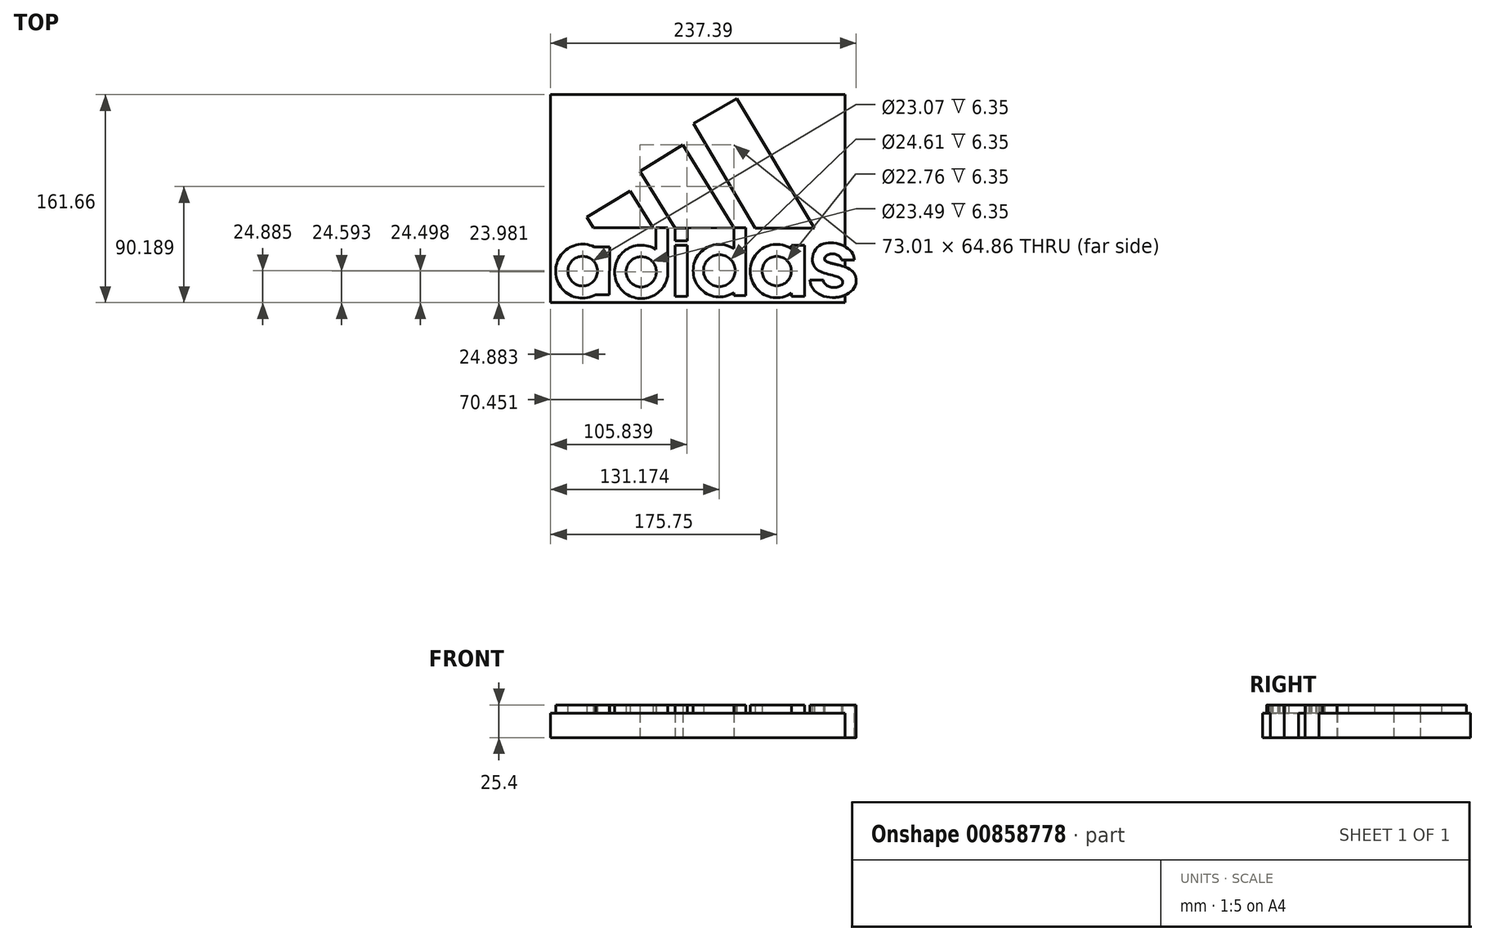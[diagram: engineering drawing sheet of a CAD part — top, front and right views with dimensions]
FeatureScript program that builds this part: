
annotation { "Feature Type Name" : "Feature", "Feature Type Description" : "" }
export const myFeature = defineFeature(function(context is Context, id is Id, definition is map)
    precondition{}
    {
        {
            var Q0;
            Q0=qCreatedBy(makeId("Top.planeOp"),FACE);
            var sketch = newSketch(context, id + "F0", { "sketchPlane" : qUnion([Q0])});
            skLineSegment(sketch, "E0", {"start": v(-125.71, -21.71) * mm, "end": v(-120.74, -29.97) * mm});
            skLineSegment(sketch, "E1", {"start": v(-120.74, -29.97) * mm, "end": v(-74.34, -29.97) * mm});
            skLineSegment(sketch, "E2", {"start": v(-125.71, -21.71) * mm, "end": v(-92.06, -1.43) * mm});
            skLineSegment(sketch, "E3", {"start": v(-92.06, -1.43) * mm, "end": v(-74.34, -30.02) * mm});
            skLineSegment(sketch, "E4", {"start": v(-84.5, 13.67) * mm, "end": v(-57.14, -30.51) * mm});
            skLineSegment(sketch, "E5", {"start": v(-84.5, 13.67) * mm, "end": v(-51.1, 34.35) * mm});
            skLineSegment(sketch, "E6", {"start": v(-51.1, 34.35) * mm, "end": v(-11.49, -30.13) * mm});
            skLineSegment(sketch, "E7", {"start": v(-57.14, -30.51) * mm, "end": v(-11.49, -30.13) * mm});
            skLineSegment(sketch, "E8", {"start": v(-42.92, 50.88) * mm, "end": v(-9.05, 70.16) * mm});
            skCircle(sketch, "E9", {"center": v(-128.95, -63.77) * mm, "radius": 11.53 * mm});
            skCircle(sketch, "E10", {"center": v(-128.95, -63.77) * mm, "radius": 20.97 * mm});
            skLineSegment(sketch, "E11", {"start": v(-107.87, -44.9) * mm, "end": v(-108.07, -82.07) * mm});
            skLineSegment(sketch, "E12", {"start": v(-107.87, -44.9) * mm, "end": v(-119.94, -44.84) * mm});
            skLineSegment(sketch, "E13", {"start": v(-108.07, -82.07) * mm, "end": v(-118.6, -82) * mm});
            skLineSegment(sketch, "E14.bottom", {"start": v(-71.98, -30.02) * mm, "end": v(-62.96, -30.02) * mm});
            skLineSegment(sketch, "E14.top", {"start": v(-71.98, -83.35) * mm, "end": v(-62.96, -83.35) * mm});
            skLineSegment(sketch, "E14.left", {"start": v(-71.98, -30.02) * mm, "end": v(-71.98, -83.35) * mm});
            skLineSegment(sketch, "E14.right", {"start": v(-62.96, -30.02) * mm, "end": v(-62.96, -83.35) * mm});
            skCircle(sketch, "E15", {"center": v(-83.38, -64.29) * mm, "radius": 11.74 * mm});
            skCircle(sketch, "E16", {"center": v(-83.38, -64.29) * mm, "radius": 20.75 * mm});
            skLineSegment(sketch, "E17.bottom", {"start": v(-57.14, -30.51) * mm, "end": v(-47.6, -30.51) * mm});
            skLineSegment(sketch, "E17.top", {"start": v(-57.14, -40.07) * mm, "end": v(-47.6, -40.07) * mm});
            skLineSegment(sketch, "E17.left", {"start": v(-57.14, -30.51) * mm, "end": v(-57.14, -40.07) * mm});
            skLineSegment(sketch, "E17.right", {"start": v(-47.6, -30.51) * mm, "end": v(-47.6, -40.07) * mm});
            skPoint(sketch, "E18.firstSnap0", {"position": v(-57.14, -35.3) * mm});
            skLineSegment(sketch, "E18.bottom", {"start": v(-57.14, -43.69) * mm, "end": v(-47.6, -43.69) * mm});
            skLineSegment(sketch, "E18.top", {"start": v(-57.14, -83.26) * mm, "end": v(-47.6, -83.26) * mm});
            skLineSegment(sketch, "E18.left", {"start": v(-57.14, -43.69) * mm, "end": v(-57.14, -83.26) * mm});
            skLineSegment(sketch, "E18.right", {"start": v(-47.6, -43.69) * mm, "end": v(-47.6, -83.26) * mm});
            skCircle(sketch, "E19", {"center": v(-22.66, -63.39) * mm, "radius": 20.38 * mm});
            skCircle(sketch, "E20", {"center": v(-22.66, -63.39) * mm, "radius": 12.3 * mm});
            skLineSegment(sketch, "E21.bottom", {"start": v(-11.49, -30.13) * mm, "end": v(-2.23, -30.13) * mm});
            skLineSegment(sketch, "E21.top", {"start": v(-11.49, -82.9) * mm, "end": v(-2.23, -82.9) * mm});
            skLineSegment(sketch, "E21.left", {"start": v(-11.49, -30.13) * mm, "end": v(-11.49, -82.9) * mm});
            skLineSegment(sketch, "E21.right", {"start": v(-2.23, -30.13) * mm, "end": v(-2.23, -82.9) * mm});
            skFitSpline(sketch, "E22", {"points": [v(47.6, -70.56) * mm, v(83.55, -71.4) * mm], "startDerivative": vector(5.7, -59.48) * mm, "endDerivative": vector(-1.15, 46.9) * mm});
            skFitSpline(sketch, "E23", {"points": [v(83.55, -71.4) * mm, v(58.96, -54.46) * mm], "startDerivative": vector(1.9, 43.78) * mm, "endDerivative": vector(-4.61, 17.28) * mm});
            skCircle(sketch, "E24", {"center": v(21.92, -63.68) * mm, "radius": 11.38 * mm});
            skCircle(sketch, "E25", {"center": v(21.92, -63.68) * mm, "radius": 20.72 * mm});
            skFitSpline(sketch, "E26", {"points": [v(58.96, -54.46) * mm, v(72.2, -55.28) * mm], "startDerivative": vector(2.24, 17.83) * mm, "endDerivative": vector(1.97, -18.22) * mm});
            skLineSegment(sketch, "E27.bottom", {"start": v(33.32, -43.65) * mm, "end": v(43.46, -43.65) * mm});
            skLineSegment(sketch, "E27.top", {"start": v(33.32, -83.48) * mm, "end": v(43.46, -83.48) * mm});
            skLineSegment(sketch, "E27.left", {"start": v(33.32, -43.65) * mm, "end": v(33.32, -83.48) * mm});
            skLineSegment(sketch, "E27.right", {"start": v(43.46, -43.65) * mm, "end": v(43.46, -83.48) * mm});
            skLineSegment(sketch, "E28", {"start": v(79.3, -45.9) * mm, "end": v(79.3, -45.9) * mm});
            skLineSegment(sketch, "E29", {"start": v(72.2, -55.19) * mm, "end": v(82.17, -55.19) * mm});
            skLineSegment(sketch, "E30", {"start": v(47.6, -70.56) * mm, "end": v(58.16, -70.56) * mm});
            skFitSpline(sketch, "E31", {"points": [v(82.17, -55.19) * mm, v(49.7, -53.69) * mm], "startDerivative": vector(1.59, 41.31) * mm, "endDerivative": vector(-5.2, -58.62) * mm});
            skFitSpline(sketch, "E32", {"points": [v(49.84, -52.58) * mm, v(73.02, -72.78) * mm], "startDerivative": vector(-8.03, -51.88) * mm, "endDerivative": vector(-3.4, -26.3) * mm});
            skFitSpline(sketch, "E33", {"points": [v(58.16, -70.56) * mm, v(73.02, -72.78) * mm], "startDerivative": vector(2.03, -24.29) * mm, "endDerivative": vector(-1.4, 13.75) * mm});
            skLineSegment(sketch, "E34", {"start": v(-9.05, 70.16) * mm, "end": v(51.14, -30.47) * mm});
            skLineSegment(sketch, "E35", {"start": v(51.14, -30.47) * mm, "end": v(5, -30.47) * mm});
            skLineSegment(sketch, "E36", {"start": v(5, -30.47) * mm, "end": v(-42.92, 50.88) * mm});
            skSolve(sketch);
        }
        {
            var Q0;
            Q0=qCreatedBy(makeId("Top.planeOp"),FACE);
            var sketch = newSketch(context, id + "F1", { "sketchPlane" : qUnion([Q0])});
            skLineSegment(sketch, "E37.bottom", {"start": v(-153.83, -88.27) * mm, "end": v(74.97, -88.27) * mm});
            skLineSegment(sketch, "E37.top", {"start": v(-153.83, 73.39) * mm, "end": v(74.97, 73.39) * mm});
            skLineSegment(sketch, "E37.left", {"start": v(-153.83, -88.27) * mm, "end": v(-153.83, 73.39) * mm});
            skLineSegment(sketch, "E37.right", {"start": v(74.97, -88.27) * mm, "end": v(74.97, 73.39) * mm});
            skSolve(sketch);
        }
        {
            var Q0;
            Q0=makeQuery(id+"F0.imprint","IMPRINT",FACE,{"disambiguationData":[TD([[makeQuery(id+"F0.imprint","IMPRINT",EDGE,{"derivedFrom":sQuery(id+"F0.wireOp",EDGE,"E4")}),1.0]])]});
            var Q1;
            Q1=makeQuery(id+"F0.imprint","IMPRINT",FACE,{"disambiguationData":[TD([[makeQuery(id+"F0.imprint","IMPRINT",EDGE,{"derivedFrom":sQuery(id+"F0.wireOp",EDGE,"E9")}),-1.0]])]});
            var Q2;
            {var subQ0=sQuery(id+"F0.wireOp",EDGE,"E0");Q2=makeQuery(id+"F0.imprint","IMPRINT",FACE,{"disambiguationData":[TD([[makeQuery(id+"F0.imprint","IMPRINT",EDGE,{"derivedFrom":subQ0}),1.0]])]});}
            var Q3;
            {var subQ0=sQuery(id+"F0.wireOp",EDGE,"E12");Q3=makeQuery(id+"F0.imprint","IMPRINT",FACE,{"disambiguationData":[TD([[makeQuery(id+"F0.imprint","IMPRINT",EDGE,{"derivedFrom":subQ0}),1.0]])]});}
            var Q4;
            {var subQ1=sQuery(id+"F0.wireOp",EDGE,"E14.left");var subQ4=sQuery(id+"F0.wireOp",EDGE,"E16");var subQ9=makeQuery(id+"F0.imprint","INTERSECT",VERTEX,{"disambiguationData":[OD(0.0)],"derivedFrom":[subQ1,subQ4]});Q4=makeQuery(id+"F0.imprint","IMPRINT",FACE,{"disambiguationData":[TD([[makeQuery(id+"F0.imprint","IMPRINT",EDGE,{"disambiguationData":[TD([[subQ9,-1.0]])],"derivedFrom":subQ1}),1.0]])]});}
            var Q5;
            {var subQ0=sQuery(id+"F0.wireOp",EDGE,"E14.bottom");Q5=makeQuery(id+"F0.imprint","IMPRINT",FACE,{"disambiguationData":[TD([[makeQuery(id+"F0.imprint","IMPRINT",EDGE,{"derivedFrom":subQ0}),-1.0]])]});}
            var Q6;
            Q6=makeQuery(id+"F0.imprint","IMPRINT",FACE,{"disambiguationData":[TD([[makeQuery(id+"F0.imprint","IMPRINT",EDGE,{"derivedFrom":sQuery(id+"F0.wireOp",EDGE,"E18.bottom")}),-1.0]])]});
            var Q7;
            {var subQ1=sQuery(id+"F0.wireOp",EDGE,"E21.bottom");Q7=makeQuery(id+"F0.imprint","IMPRINT",FACE,{"disambiguationData":[TD([[makeQuery(id+"F0.imprint","IMPRINT",EDGE,{"derivedFrom":subQ1}),-1.0]])]});}
            var Q8;
            {var subQ0=sQuery(id+"F0.wireOp",EDGE,"E21.left");var subQ1=sQuery(id+"F0.wireOp",EDGE,"E19");var subQ2=makeQuery(id+"F0.imprint","INTERSECT",VERTEX,{"disambiguationData":[OD(0.0)],"derivedFrom":[subQ1,subQ0]});Q8=makeQuery(id+"F0.imprint","IMPRINT",FACE,{"disambiguationData":[TD([[makeQuery(id+"F0.imprint","IMPRINT",EDGE,{"disambiguationData":[TD([[subQ2,-1.0]])],"derivedFrom":subQ1}),1.0]])]});}
            var Q9;
            {var subQ0=sQuery(id+"F0.wireOp",EDGE,"E21.left");var subQ1=sQuery(id+"F0.wireOp",EDGE,"E19");var subQ2=makeQuery(id+"F0.imprint","INTERSECT",VERTEX,{"disambiguationData":[OD(0.0)],"derivedFrom":[subQ1,subQ0]});Q9=makeQuery(id+"F0.imprint","IMPRINT",FACE,{"disambiguationData":[TD([[makeQuery(id+"F0.imprint","IMPRINT",EDGE,{"disambiguationData":[TD([[subQ2,1.0]])],"derivedFrom":subQ1}),1.0]])]});}
            var Q10;
            {var subQ0=sQuery(id+"F0.wireOp",EDGE,"E13");Q10=makeQuery(id+"F0.imprint","IMPRINT",FACE,{"disambiguationData":[TD([[makeQuery(id+"F0.imprint","IMPRINT",EDGE,{"derivedFrom":subQ0}),-1.0]])]});}
            var Q11;
            Q11=makeQuery(id+"F0.imprint","IMPRINT",FACE,{"disambiguationData":[TD([[makeQuery(id+"F0.imprint","IMPRINT",EDGE,{"derivedFrom":sQuery(id+"F0.wireOp",EDGE,"E24")}),-1.0]])]});
            var Q12;
            {var subQ0=sQuery(id+"F0.wireOp",EDGE,"E27.left");var subQ1=sQuery(id+"F0.wireOp",EDGE,"E25");var subQ2=makeQuery(id+"F0.imprint","INTERSECT",VERTEX,{"disambiguationData":[OD(0.0)],"derivedFrom":[subQ1,subQ0]});Q12=makeQuery(id+"F0.imprint","IMPRINT",FACE,{"disambiguationData":[TD([[makeQuery(id+"F0.imprint","IMPRINT",EDGE,{"disambiguationData":[TD([[subQ2,1.0]])],"derivedFrom":subQ1}),1.0]])]});}
            var Q13;
            {var subQ1=sQuery(id+"F0.wireOp",EDGE,"E27.bottom");Q13=makeQuery(id+"F0.imprint","IMPRINT",FACE,{"disambiguationData":[TD([[makeQuery(id+"F0.imprint","IMPRINT",EDGE,{"derivedFrom":subQ1}),-1.0]])]});}
            var Q14;
            Q14=makeQuery(id+"F0.imprint","IMPRINT",FACE,{"disambiguationData":[TD([[makeQuery(id+"F0.imprint","IMPRINT",EDGE,{"derivedFrom":sQuery(id+"F0.wireOp",EDGE,"E22")}),1.0]])]});
            var Q15;
            Q15=makeQuery(id+"F0.imprint","IMPRINT",FACE,{"disambiguationData":[TD([[makeQuery(id+"F0.imprint","IMPRINT",EDGE,{"derivedFrom":sQuery(id+"F0.wireOp",EDGE,"E8")}),-1.0]])]});
            var Q16;
            {var subQ0=sQuery(id+"F0.wireOp",EDGE,"E16");var subQ1=sQuery(id+"F0.wireOp",EDGE,"E14.left");var subQ2=makeQuery(id+"F0.imprint","INTERSECT",VERTEX,{"disambiguationData":[OD(0.0)],"derivedFrom":[subQ1,subQ0]});Q16=makeQuery(id+"F0.imprint","IMPRINT",FACE,{"disambiguationData":[TD([[makeQuery(id+"F0.imprint","IMPRINT",EDGE,{"disambiguationData":[TD([[subQ2,-1.0]])],"derivedFrom":subQ1}),-1.0]])]});}
            var Q17;
            Q17=makeQuery(id+"F0.imprint","IMPRINT",FACE,{"disambiguationData":[TD([[makeQuery(id+"F0.imprint","IMPRINT",EDGE,{"derivedFrom":sQuery(id+"F0.wireOp",EDGE,"E17.bottom")}),-1.0]])]});
            extrude(context, id + "F2", {"entities" : qUnion([Q0, Q1, Q2, Q3, Q4, Q5, Q6, Q7, Q8, Q9, Q10, Q11, Q12, Q13, Q14, Q15, Q16, Q17]), "depth" : 25.4 * mm, "offsetDistance" : 25.4 * mm});
        }
        {
            var Q0;
            Q0=makeQuery(id+"F1.imprint","IMPRINT",FACE,{"disambiguationData":[TD([[makeQuery(id+"F1.imprint","IMPRINT",EDGE,{"derivedFrom":sQuery(id+"F1.wireOp",EDGE,"E37.bottom")}),1.0]])]});
            extrude(context, id + "F3", {"entities" : qUnion([Q0]), "operationType" : NewBodyOperationType.ADD, "depth" : 19.05 * mm, "offsetDistance" : 25.4 * mm});
        }
    });
